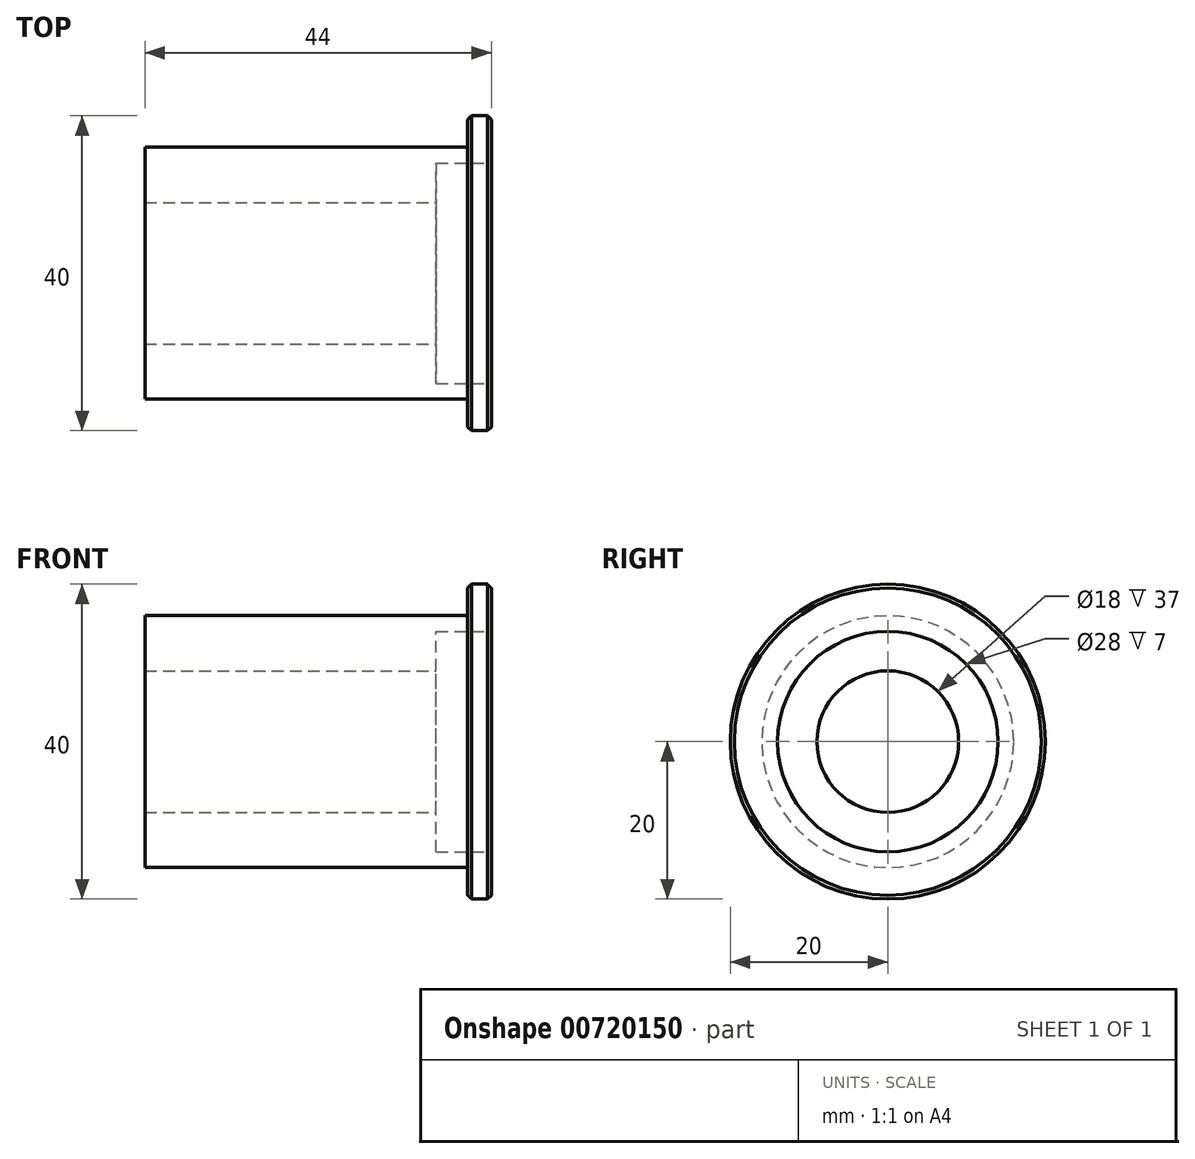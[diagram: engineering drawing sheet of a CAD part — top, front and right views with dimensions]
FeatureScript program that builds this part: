
annotation { "Feature Type Name" : "Feature", "Feature Type Description" : "" }
export const myFeature = defineFeature(function(context is Context, id is Id, definition is map)
    precondition{}
    {
        {
            var Q0;
            Q0=qCreatedBy(makeId("Front.planeOp"),FACE);
            var sketch = newSketch(context, id + "F0", { "sketchPlane" : qUnion([Q0])});
            skLineSegment(sketch, "E0", {"start": v(0, 9) * mm, "end": v(0, 16) * mm});
            skLineSegment(sketch, "E1", {"start": v(0, 16) * mm, "end": v(41, 16) * mm});
            skLineSegment(sketch, "E2", {"start": v(41, 16) * mm, "end": v(41, 20) * mm});
            skLineSegment(sketch, "E3", {"start": v(41, 20) * mm, "end": v(44, 20) * mm});
            skLineSegment(sketch, "E4", {"start": v(44, 20) * mm, "end": v(44, 14) * mm});
            skLineSegment(sketch, "E5", {"start": v(44, 0) * mm, "end": v(0, 0) * mm});
            skLineSegment(sketch, "E6.0", {"start": v(37, 9) * mm, "end": v(0, 9) * mm});
            skLineSegment(sketch, "E7.0", {"start": v(37, 14) * mm, "end": v(37, 9) * mm});
            skLineSegment(sketch, "E8.0", {"start": v(44, 14) * mm, "end": v(37, 14) * mm});
            skSolve(sketch);
        }
        {
            var Q0;
            Q0=makeQuery(id+"F0.imprint","IMPRINT",FACE,{"disambiguationData":[TD([[makeQuery(id+"F0.imprint","IMPRINT",EDGE,{"derivedFrom":sQuery(id+"F0.wireOp",EDGE,"E0")}),-1.0]])]});
            var Q1;
            Q1=sQuery(id+"F0.wireOp",EDGE,"E5");
            revolve(context, id + "F1", {"surfaceOperationType" : NewSurfaceOperationType.NEW, "entities" : qUnion([Q0]), "axis" : qUnion([Q1]), "revolveType" : RevolveType.FULL});
        }
        {
            var Q0;
            Q0=makeQuery(id+"F1.opRevolve","SWEPT_EDGE",EDGE,{"disambiguationData":[OSD([sQuery(id+"F0.wireOp",EDGE,"E2"),sQuery(id+"F0.wireOp",EDGE,"E3")])]});
            var Q1;
            Q1=makeQuery(id+"F1.opRevolve","SWEPT_EDGE",EDGE,{"disambiguationData":[OSD([sQuery(id+"F0.wireOp",EDGE,"E3"),sQuery(id+"F0.wireOp",EDGE,"E4")])]});
            chamfer(context, id + "F2", {"entities" : qUnion([Q0, Q1]), "width" : .5 * mm, "tangentPropagation" : true});
        }
    });
